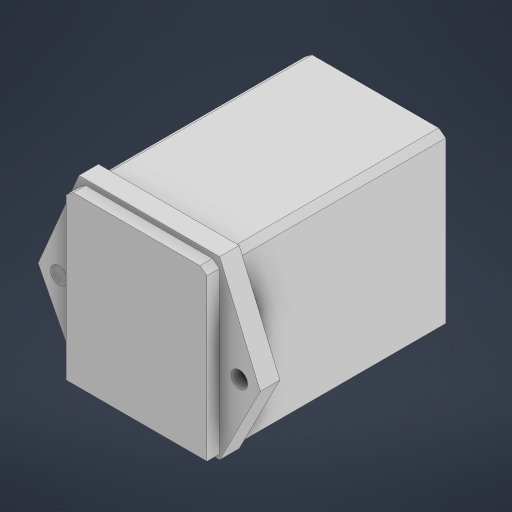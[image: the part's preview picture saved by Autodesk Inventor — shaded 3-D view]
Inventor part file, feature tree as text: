
AUTODESK INVENTOR PART (.ipt)
format: ipt  version: 2024 (Build 280153000, 153)  size: 189,952 bytes
history: native  units: mm
features: extrude x3, other x1, sketch x1
ambient origin geometry x8: Origin, YZ Plane, XZ Plane, XY Plane, X Axis, Y Axis, Z Axis, Center Point
bodies: Body1 (feature_tree)
feature tree (5):
  other  "솔리드1"
  sketch  "스케치1"
  extrude  "돌출1"  Depth=28.0mm
  extrude  "돌출2"  Depth=33.0mm
  extrude  "돌출3"  Depth=28.0mm
